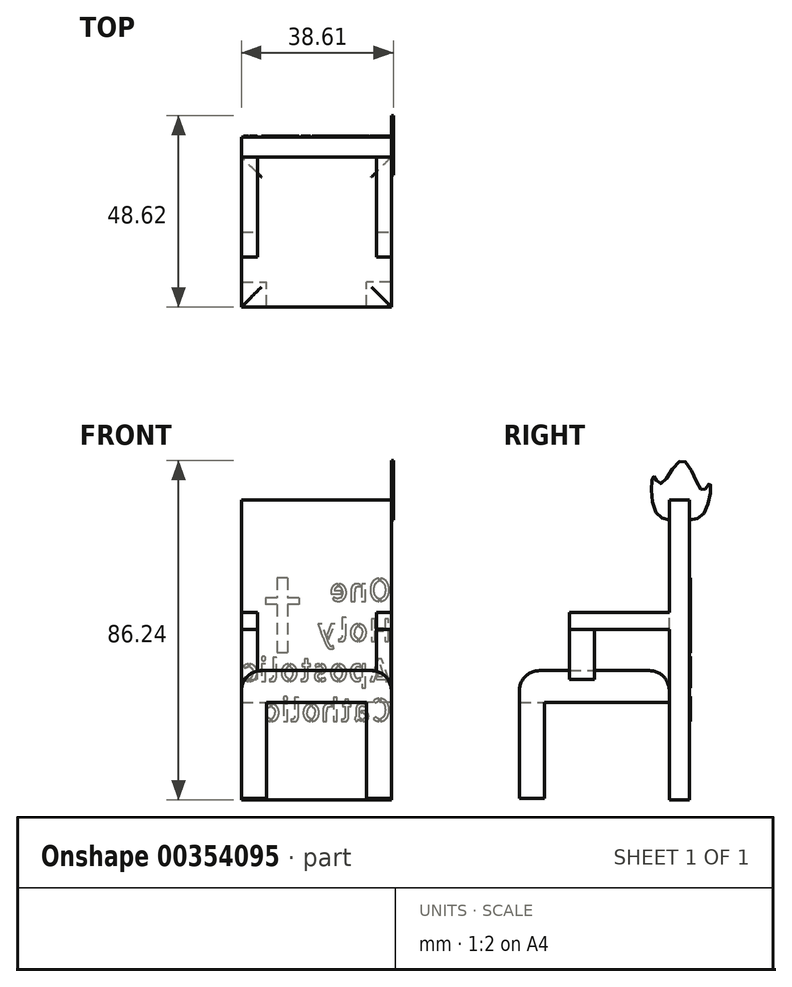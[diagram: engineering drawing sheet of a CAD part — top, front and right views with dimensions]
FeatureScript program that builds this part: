
annotation { "Feature Type Name" : "Feature", "Feature Type Description" : "" }
export const myFeature = defineFeature(function(context is Context, id is Id, definition is map)
    precondition{}
    {
        {
            var Q0;
            Q0=qCreatedBy(makeId("Top.planeOp"),FACE);
            var sketch = newSketch(context, id + "F0", { "sketchPlane" : qUnion([Q0])});
            skLineSegment(sketch, "E0.bottom", {"start": v(0, 0) * mm, "end": v(38.1, 0) * mm});
            skLineSegment(sketch, "E0.top", {"start": v(0, 5.08) * mm, "end": v(38.1, 5.08) * mm});
            skLineSegment(sketch, "E0.left", {"start": v(0, 0) * mm, "end": v(0, 5.08) * mm});
            skLineSegment(sketch, "E0.right", {"start": v(38.1, 0) * mm, "end": v(38.1, 5.08) * mm});
            skSolve(sketch);
        }
        {
            var Q0;
            Q0=makeQuery(id+"F0.imprint","IMPRINT",FACE,{"disambiguationData":[TD([[makeQuery(id+"F0.imprint","IMPRINT",EDGE,{"derivedFrom":sQuery(id+"F0.wireOp",EDGE,"E0.bottom")}),1.0]])]});
            extrude(context, id + "F1", {"entities" : qUnion([Q0]), "depth" : 76.2 * mm});
        }
        {
            var Q0;
            Q0=makeQuery(id+"F1.opExtrude","SWEPT_FACE",FACE,{"disambiguationData":[OSD([sQuery(id+"F0.wireOp",EDGE,"E0.bottom")])]});
            var sketch = newSketch(context, id + "F2", { "sketchPlane" : qUnion([Q0])});
            skSolve(sketch);
        }
        {
            var Q0;
            {var subQ0=sQuery(id+"F0.wireOp",EDGE,"E0.bottom");Q0=makeQuery(id+"F2.imprint","IMPRINT",FACE,{"disambiguationData":[TD([[makeQuery(id+"F2.imprint","IMPRINT",EDGE,{"derivedFrom":makeQuery(id+"F1.opExtrude","CAP_EDGE",EDGE,{"disambiguationData":[OSD([subQ0])],"isStart":true})}),1.0]])]});}
            var sketch = newSketch(context, id + "F3", { "sketchPlane" : qUnion([Q0])});
            skLineSegment(sketch, "E1.bottom", {"start": v(0, 24.76) * mm, "end": v(38.1, 24.76) * mm});
            skLineSegment(sketch, "E1.top", {"start": v(0, 32.85) * mm, "end": v(38.1, 32.85) * mm});
            skLineSegment(sketch, "E1.left", {"start": v(0, 24.76) * mm, "end": v(0, 32.85) * mm});
            skLineSegment(sketch, "E1.right", {"start": v(38.1, 24.76) * mm, "end": v(38.1, 32.85) * mm});
            skSolve(sketch);
        }
        {
            var Q0;
            Q0=makeQuery(id+"F3.imprint","IMPRINT",FACE,{"disambiguationData":[TD([[makeQuery(id+"F3.imprint","IMPRINT",EDGE,{"derivedFrom":sQuery(id+"F3.wireOp",EDGE,"E1.bottom")}),1.0]])]});
            extrude(context, id + "F4", {"entities" : qUnion([Q0]), "depth" : 38.1 * mm});
        }
        {
            var Q0;
            Q0=makeQuery(id+"F4.opExtrude","SWEPT_FACE",FACE,{"disambiguationData":[OSD([sQuery(id+"F3.wireOp",EDGE,"E1.bottom")])]});
            var sketch = newSketch(context, id + "F5", { "sketchPlane" : qUnion([Q0])});
            skLineSegment(sketch, "E2.bottom", {"start": v(0, 38.1) * mm, "end": v(6.35, 38.1) * mm});
            skLineSegment(sketch, "E2.top", {"start": v(0, 31.75) * mm, "end": v(6.35, 31.75) * mm});
            skLineSegment(sketch, "E2.left", {"start": v(0, 38.1) * mm, "end": v(0, 31.75) * mm});
            skLineSegment(sketch, "E2.right", {"start": v(6.35, 38.1) * mm, "end": v(6.35, 31.75) * mm});
            skLineSegment(sketch, "E3.bottom", {"start": v(38.1, 38.1) * mm, "end": v(31.75, 38.1) * mm});
            skLineSegment(sketch, "E3.top", {"start": v(38.1, 31.75) * mm, "end": v(31.75, 31.75) * mm});
            skLineSegment(sketch, "E3.left", {"start": v(38.1, 38.1) * mm, "end": v(38.1, 31.75) * mm});
            skLineSegment(sketch, "E3.right", {"start": v(31.75, 38.1) * mm, "end": v(31.75, 31.75) * mm});
            skLineSegment(sketch, "E4.bottom", {"start": v(0, 0) * mm, "end": v(6.35, 0) * mm});
            skLineSegment(sketch, "E4.top", {"start": v(0, 6.35) * mm, "end": v(6.35, 6.35) * mm});
            skLineSegment(sketch, "E4.left", {"start": v(0, 0) * mm, "end": v(0, 6.35) * mm});
            skLineSegment(sketch, "E4.right", {"start": v(6.35, 0) * mm, "end": v(6.35, 6.35) * mm});
            skLineSegment(sketch, "E5.bottom", {"start": v(38.1, 0) * mm, "end": v(31.75, 0) * mm});
            skLineSegment(sketch, "E5.top", {"start": v(38.1, 6.35) * mm, "end": v(31.75, 6.35) * mm});
            skLineSegment(sketch, "E5.left", {"start": v(38.1, 0) * mm, "end": v(38.1, 6.35) * mm});
            skLineSegment(sketch, "E5.right", {"start": v(31.75, 0) * mm, "end": v(31.75, 6.35) * mm});
            skSolve(sketch);
        }
        {
            var Q0;
            Q0=makeQuery(id+"F5.imprint","IMPRINT",FACE,{"disambiguationData":[TD([[makeQuery(id+"F5.imprint","IMPRINT",EDGE,{"derivedFrom":sQuery(id+"F5.wireOp",EDGE,"E2.bottom")}),-1.0]])]});
            var Q1;
            Q1=makeQuery(id+"F5.imprint","IMPRINT",FACE,{"disambiguationData":[TD([[makeQuery(id+"F5.imprint","IMPRINT",EDGE,{"derivedFrom":sQuery(id+"F5.wireOp",EDGE,"E3.bottom")}),-1.0]])]});
            extrude(context, id + "F6", {"entities" : qUnion([Q0, Q1]), "operationType" : NewBodyOperationType.ADD, "depth" : 24.38 * mm});
        }
        {
            var Q0;
            Q0=makeQuery(id+"F4.opExtrude","SWEPT_FACE",FACE,{"disambiguationData":[OSD([sQuery(id+"F3.wireOp",EDGE,"E1.top")])]});
            fillet(context, id + "F7", {"entities" : qUnion([Q0]), "radius" : 5.08 * mm, "tangentPropagation" : true, "allowEdgeOverflow" : false});
        }
        {
            var Q0;
            {var subQ0=sQuery(id+"F0.wireOp",EDGE,"E0.bottom");Q0=makeQuery(id+"F2.imprint","IMPRINT",FACE,{"disambiguationData":[TD([[makeQuery(id+"F2.imprint","IMPRINT",EDGE,{"derivedFrom":makeQuery(id+"F1.opExtrude","CAP_EDGE",EDGE,{"disambiguationData":[OSD([subQ0])],"isStart":true})}),1.0]])]});}
            var sketch = newSketch(context, id + "F8", { "sketchPlane" : qUnion([Q0])});
            skLineSegment(sketch, "E6.bottom", {"start": v(0, 47.58) * mm, "end": v(4.03, 47.58) * mm});
            skLineSegment(sketch, "E6.top", {"start": v(0, 43.26) * mm, "end": v(4.03, 43.26) * mm});
            skLineSegment(sketch, "E6.left", {"start": v(0, 47.58) * mm, "end": v(0, 43.26) * mm});
            skLineSegment(sketch, "E6.right", {"start": v(4.03, 47.58) * mm, "end": v(4.03, 43.26) * mm});
            skLineSegment(sketch, "E7.bottom", {"start": v(38.13, 43.26) * mm, "end": v(34.32, 43.26) * mm});
            skLineSegment(sketch, "E7.top", {"start": v(38.13, 47.58) * mm, "end": v(34.32, 47.58) * mm});
            skLineSegment(sketch, "E7.left", {"start": v(38.13, 43.26) * mm, "end": v(38.13, 47.58) * mm});
            skLineSegment(sketch, "E7.right", {"start": v(34.32, 43.26) * mm, "end": v(34.32, 47.58) * mm});
            skSolve(sketch);
        }
        {
            var Q0;
            {var subQ0=sQuery(id+"F8.wireOp",EDGE,"E7.right");Q0=makeQuery(id+"F8.imprint","IMPRINT",FACE,{"disambiguationData":[TD([[makeQuery(id+"F8.imprint","IMPRINT",EDGE,{"derivedFrom":subQ0}),-1.0]])]});}
            var Q1;
            Q1=makeQuery(id+"F8.imprint","IMPRINT",FACE,{"disambiguationData":[TD([[makeQuery(id+"F8.imprint","IMPRINT",EDGE,{"derivedFrom":sQuery(id+"F8.wireOp",EDGE,"E6.bottom")}),-1.0]])]});
            extrude(context, id + "F9", {"entities" : qUnion([Q0, Q1]), "operationType" : NewBodyOperationType.ADD, "depth" : 25.4 * mm});
        }
        {
            var Q0;
            Q0=makeQuery(id+"F9.opExtrude","SWEPT_FACE",FACE,{"disambiguationData":[OSD([sQuery(id+"F8.wireOp",EDGE,"E6.top")])]});
            var sketch = newSketch(context, id + "F10", { "sketchPlane" : qUnion([Q0])});
            skLineSegment(sketch, "E8.bottom", {"start": v(0, 25.4) * mm, "end": v(4.03, 25.4) * mm});
            skLineSegment(sketch, "E8.top", {"start": v(0, 19.05) * mm, "end": v(4.03, 19.05) * mm});
            skLineSegment(sketch, "E8.left", {"start": v(0, 25.4) * mm, "end": v(0, 19.05) * mm});
            skLineSegment(sketch, "E8.right", {"start": v(4.03, 25.4) * mm, "end": v(4.03, 19.05) * mm});
            skLineSegment(sketch, "E9.bottom", {"start": v(34.3, 25.4) * mm, "end": v(38.06, 25.4) * mm});
            skLineSegment(sketch, "E9.top", {"start": v(34.3, 19.05) * mm, "end": v(38.06, 19.05) * mm});
            skLineSegment(sketch, "E9.left", {"start": v(34.3, 25.4) * mm, "end": v(34.3, 19.05) * mm});
            skLineSegment(sketch, "E9.right", {"start": v(38.06, 25.4) * mm, "end": v(38.06, 19.05) * mm});
            skSolve(sketch);
        }
        {
            var Q0;
            Q0 = qSketchRegion(id + "F10", true);
            extrude(context, id + "F11", {"entities" : qUnion([Q0]), "depth" : 12.7 * mm});
        }
        {
            var Q0;
            {var subQ0=sQuery(id+"F0.wireOp",EDGE,"E0.right");Q0=makeQuery(id+"F9.boolean.opBoolean","MERGE",FACE,{"derivedFrom":[makeQuery(id+"F1.opExtrude","SWEPT_FACE",FACE,{"disambiguationData":[OSD([subQ0])]}),makeQuery(id+"F9.opExtrude","SWEPT_FACE",FACE,{"disambiguationData":[OSD([sQuery(id+"F0.wireOp",EDGE,"E0.bottom"),subQ0])]})]});}
            var sketch = newSketch(context, id + "F12", { "sketchPlane" : qUnion([Q0])});
            skPoint(sketch, "E10.0.internal.snap0", {"position": v(2.54, 76.2) * mm});
            skFitSpline(sketch, "E10", {"points": [v(2.54, 71.2) * mm, v(8.89, 72.96) * mm, v(10.25, 80.43) * mm, v(8.49, 78.66) * mm, v(3.36, 86.24) * mm, v(-2.28, 80.37) * mm, v(-4.05, 82.2) * mm, v(-3.42, 73.02) * mm, v(2.54, 71.2) * mm]});
            skSolve(sketch);
        }
        {
            var Q0;
            {var subQ1=sQuery(id+"F0.wireOp",EDGE,"E0.right");var subQ8=makeQuery(id+"F1.opExtrude","CAP_EDGE",EDGE,{"disambiguationData":[OSD([subQ1])],"isStart":false});Q0=makeQuery(id+"F12.imprint","IMPRINT",FACE,{"disambiguationData":[TD([[makeQuery(id+"F12.imprint","IMPRINT",EDGE,{"derivedFrom":subQ8}),1.0]])]});}
            extrude(context, id + "F13", {"entities" : qUnion([Q0]), "depth" : 0.5 * mm});
        }
        {
            var Q0;
            Q0=makeQuery(id+"F1.opExtrude","SWEPT_FACE",FACE,{"disambiguationData":[OSD([sQuery(id+"F0.wireOp",EDGE,"E0.top")])]});
            var sketch = newSketch(context, id + "F14", { "sketchPlane" : qUnion([Q0])});
            skText(sketch, "E11", { "text": "One\nHoly\nApostolic\nCatholic", "fontName": "AllertaStencil-Regular.ttf"});
            const initialGuessF14  = {"E11": [-0.0381, 0.05048, 1, 0, 0.00572]};
            skSetInitialGuess(sketch, initialGuessF14);
            skSolve(sketch);
        }
        {
            var Q0;
            Q0 = qSketchRegion(id + "F14", true);
            extrude(context, id + "F15", {"entities" : qUnion([Q0]), "operationType" : NewBodyOperationType.ADD, "depth" : 0.25 * mm});
        }
        {
            var Q0;
            {var subQ1=sQuery(id+"F0.wireOp",EDGE,"E0.left");var subQ2=sQuery(id+"F0.wireOp",EDGE,"E0.top");Q0=makeQuery(id+"F15.boolean.opBoolean","SPLIT",FACE,{"disambiguationData":[TD([makeQuery(id+"F1.opExtrude","SWEPT_FACE",FACE,{"disambiguationData":[OSD([subQ1])]})])],"derivedFrom":makeQuery(id+"F1.opExtrude","SWEPT_FACE",FACE,{"disambiguationData":[OSD([subQ2])]})});}
            var sketch = newSketch(context, id + "F16", { "sketchPlane" : qUnion([Q0])});
            skLineSegment(sketch, "E12.bottom", {"start": v(-11.68, 56.37) * mm, "end": v(-9.05, 56.37) * mm});
            skLineSegment(sketch, "E12.top", {"start": v(-11.68, 37.3) * mm, "end": v(-9.05, 37.3) * mm});
            skLineSegment(sketch, "E12.left", {"start": v(-11.68, 56.37) * mm, "end": v(-11.68, 37.3) * mm});
            skLineSegment(sketch, "E12.right", {"start": v(-9.05, 56.37) * mm, "end": v(-9.05, 37.3) * mm});
            skLineSegment(sketch, "E13.bottom", {"start": v(-14.61, 51.3) * mm, "end": v(-6.07, 51.3) * mm});
            skLineSegment(sketch, "E13.top", {"start": v(-14.61, 49.62) * mm, "end": v(-6.07, 49.62) * mm});
            skLineSegment(sketch, "E13.left", {"start": v(-14.61, 51.3) * mm, "end": v(-14.61, 49.62) * mm});
            skLineSegment(sketch, "E13.right", {"start": v(-6.07, 51.3) * mm, "end": v(-6.07, 49.62) * mm});
            skSolve(sketch);
        }
        {
            var Q0;
            {var subQ0=sQuery(id+"F16.wireOp",EDGE,"E12.bottom");Q0=makeQuery(id+"F16.imprint","IMPRINT",FACE,{"disambiguationData":[TD([[makeQuery(id+"F16.imprint","IMPRINT",EDGE,{"derivedFrom":subQ0}),-1.0]])]});}
            var Q1;
            {var subQ5=sQuery(id+"F16.wireOp",EDGE,"E13.left");Q1=makeQuery(id+"F16.imprint","IMPRINT",FACE,{"disambiguationData":[TD([[makeQuery(id+"F16.imprint","IMPRINT",EDGE,{"derivedFrom":subQ5}),1.0]])]});}
            var Q2;
            {var subQ0=sQuery(id+"F16.wireOp",EDGE,"E13.bottom");var subQ1=sQuery(id+"F16.wireOp",EDGE,"E12.left");var subQ2=makeQuery(id+"F16.imprint","INTERSECT",VERTEX,{"derivedFrom":[subQ1,subQ0]});Q2=makeQuery(id+"F16.imprint","IMPRINT",FACE,{"disambiguationData":[TD([[makeQuery(id+"F16.imprint","IMPRINT",EDGE,{"disambiguationData":[TD([[subQ2,-1.0]])],"derivedFrom":subQ1}),1.0]])]});}
            var Q3;
            {var subQ0=sQuery(id+"F16.wireOp",EDGE,"E12.top");Q3=makeQuery(id+"F16.imprint","IMPRINT",FACE,{"disambiguationData":[TD([[makeQuery(id+"F16.imprint","IMPRINT",EDGE,{"derivedFrom":subQ0}),1.0]])]});}
            var Q4;
            {var subQ5=sQuery(id+"F16.wireOp",EDGE,"E13.right");Q4=makeQuery(id+"F16.imprint","IMPRINT",FACE,{"disambiguationData":[TD([[makeQuery(id+"F16.imprint","IMPRINT",EDGE,{"derivedFrom":subQ5}),-1.0]])]});}
            extrude(context, id + "F17", {"entities" : qUnion([Q0, Q1, Q2, Q3, Q4]), "operationType" : NewBodyOperationType.ADD, "depth" : 0.25 * mm});
        }
    });
